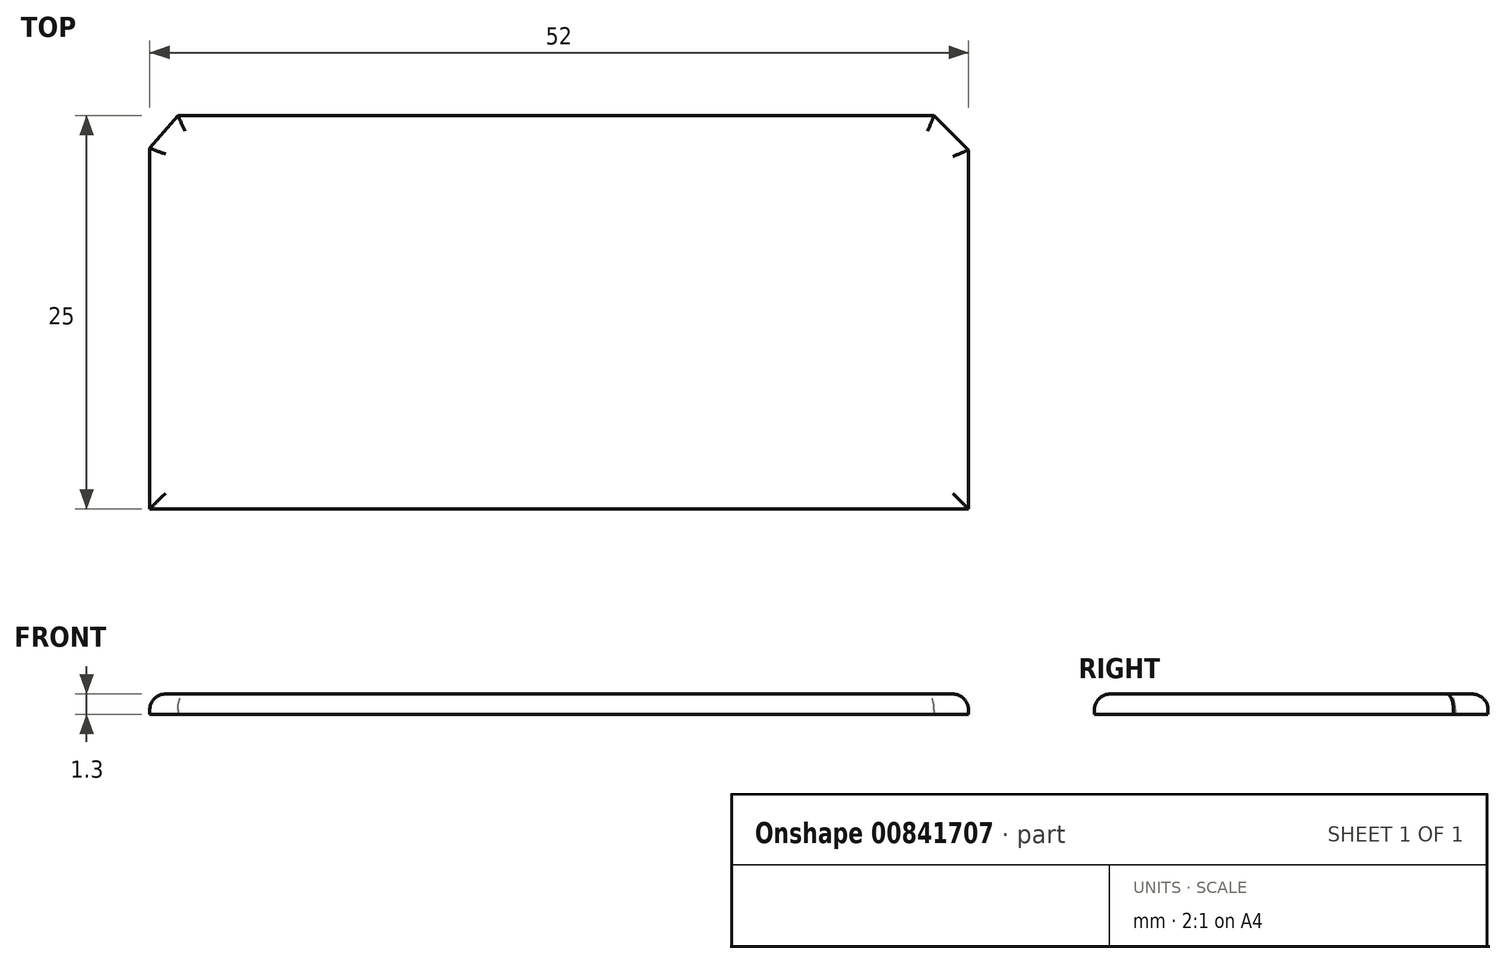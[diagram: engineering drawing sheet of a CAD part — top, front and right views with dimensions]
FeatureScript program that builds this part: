
annotation { "Feature Type Name" : "Feature", "Feature Type Description" : "" }
export const myFeature = defineFeature(function(context is Context, id is Id, definition is map)
    precondition{}
    {
        {
            var Q0;
            Q0=qCreatedBy(makeId("Top.planeOp"),FACE);
            var sketch = newSketch(context, id + "F0", { "sketchPlane" : qUnion([Q0])});
            skLineSegment(sketch, "E0.bottom", {"start": v(26, 12.5) * mm, "end": v(-26, 12.5) * mm});
            skLineSegment(sketch, "E0.top", {"start": v(26, -12.5) * mm, "end": v(-26, -12.5) * mm});
            skLineSegment(sketch, "E0.left", {"start": v(26, 12.5) * mm, "end": v(26, -12.5) * mm});
            skLineSegment(sketch, "E0.right", {"start": v(-26, 12.5) * mm, "end": v(-26, -12.5) * mm});
            skPoint(sketch, "E0.middle", {"position": v(0, 0) * mm});
            skLineSegment(sketch, "E1", {"start": v(-26, 10.42) * mm, "end": v(-24.21, 12.5) * mm});
            skLineSegment(sketch, "E2", {"start": v(26, 10.3) * mm, "end": v(23.82, 12.5) * mm});
            skSolve(sketch);
        }
        {
            var Q0;
            {var subQ1=sQuery(id+"F0.wireOp",EDGE,"E0.top");Q0=makeQuery(id+"F0.imprint","IMPRINT",FACE,{"disambiguationData":[TD([[makeQuery(id+"F0.imprint","IMPRINT",EDGE,{"derivedFrom":subQ1}),-1.0]])]});}
            extrude(context, id + "F1", {"entities" : qUnion([Q0]), "depth" : 1.3 * mm, "offsetDistance" : 25 * mm});
        }
        {
            var Q0;
            Q0=makeQuery(id+"F1.opExtrude","CAP_FACE",FACE,{"disambiguationData":[OSD([sQuery(id+"F0.wireOp",EDGE,"E0.bottom"),sQuery(id+"F0.wireOp",EDGE,"E0.top"),sQuery(id+"F0.wireOp",EDGE,"E0.left"),sQuery(id+"F0.wireOp",EDGE,"E0.right")])],"isStart":false});
            fillet(context, id + "F2", {"entities" : qUnion([Q0]), "radius" : 1 * mm, "tangentPropagation" : true, "allowEdgeOverflow" : false});
        }
    });
